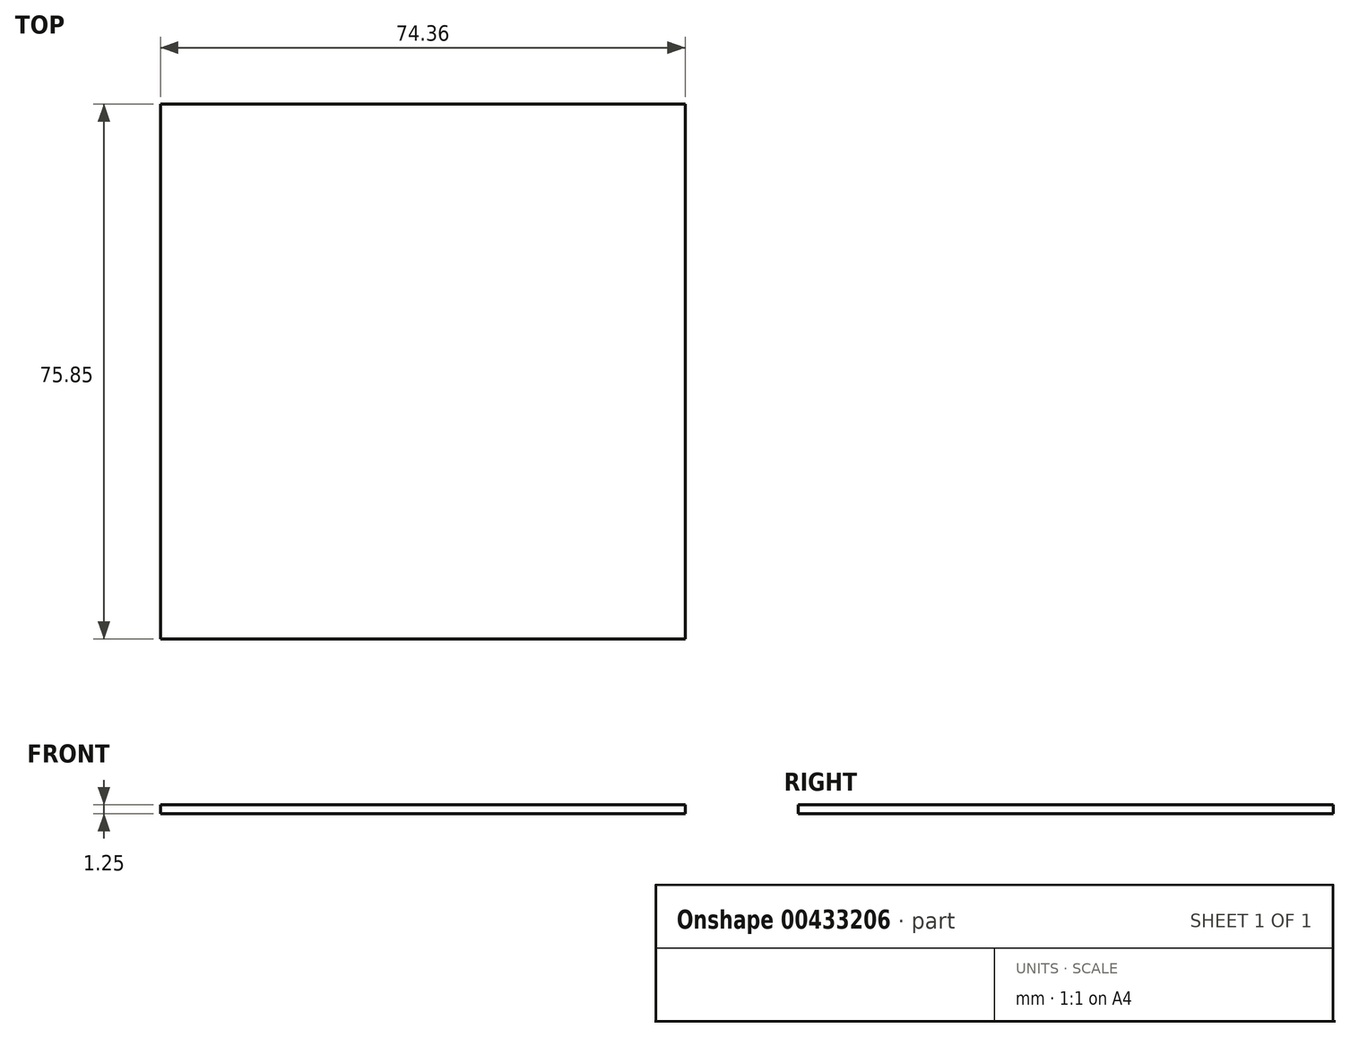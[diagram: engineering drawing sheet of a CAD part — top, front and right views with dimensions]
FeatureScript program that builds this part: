
annotation { "Feature Type Name" : "Feature", "Feature Type Description" : "" }
export const myFeature = defineFeature(function(context is Context, id is Id, definition is map)
    precondition{}
    {
        {
            var Q0;
            Q0=qCreatedBy(makeId("Top.planeOp"),FACE);
            var sketch = newSketch(context, id + "F0", { "sketchPlane" : qUnion([Q0])});
            skLineSegment(sketch, "E0.bottom", {"start": v(74.36, 0) * mm, "end": v(0, 0) * mm});
            skLineSegment(sketch, "E0.top", {"start": v(74.36, 75.85) * mm, "end": v(0, 75.85) * mm});
            skLineSegment(sketch, "E0.left", {"start": v(74.36, 0) * mm, "end": v(74.36, 75.85) * mm});
            skLineSegment(sketch, "E0.right", {"start": v(0, 0) * mm, "end": v(0, 75.85) * mm});
            skSolve(sketch);
        }
        {
            var Q0;
            Q0=makeQuery(id+"F0.imprint","IMPRINT",FACE,{"disambiguationData":[TD([[makeQuery(id+"F0.imprint","IMPRINT",EDGE,{"derivedFrom":sQuery(id+"F0.wireOp",EDGE,"E0.bottom")}),-1.0]])]});
            extrude(context, id + "F1", {"entities" : qUnion([Q0]), "depth" : 1.25 * mm});
        }
    });
